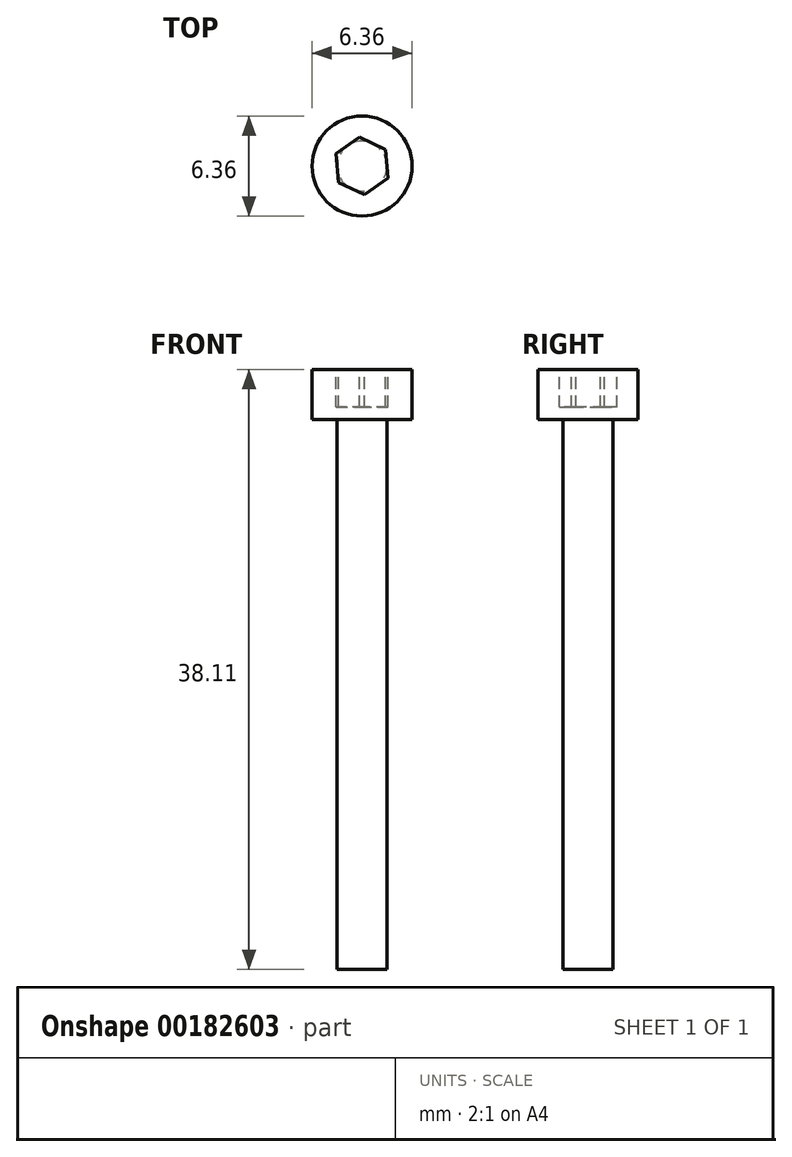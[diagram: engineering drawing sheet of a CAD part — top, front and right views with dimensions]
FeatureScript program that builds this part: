
annotation { "Feature Type Name" : "Feature", "Feature Type Description" : "" }
export const myFeature = defineFeature(function(context is Context, id is Id, definition is map)
    precondition{}
    {
        {
            var Q0;
            Q0=qCreatedBy(makeId("Top.planeOp"),FACE);
            var sketch = newSketch(context, id + "F0", { "sketchPlane" : qUnion([Q0])});
            skCircle(sketch, "E0", {"center": v(0, 0) * mm, "radius": 3.18 * mm});
            skSolve(sketch);
        }
        {
            var Q0;
            Q0 = qSketchRegion(id + "F0", true);
            extrude(context, id + "F1", {"entities" : qUnion([Q0]), "depth" : 3.17 * mm});
        }
        {
            var Q0;
            Q0=makeQuery(id+"F1.opExtrude","CAP_FACE",FACE,{"disambiguationData":[OSD([sQuery(id+"F0.wireOp",EDGE,"E0")])],"isStart":true});
            var sketch = newSketch(context, id + "F2", { "sketchPlane" : qUnion([Q0])});
            skCircle(sketch, "E1", {"center": v(0, 0) * mm, "radius": 1.59 * mm});
            skSolve(sketch);
        }
        {
            var Q0;
            Q0 = qSketchRegion(id + "F2", true);
            extrude(context, id + "F3", {"entities" : qUnion([Q0]), "operationType" : NewBodyOperationType.ADD, "depth" : 34.92 * mm});
        }
        {
            var Q0;
            Q0=makeQuery(id+"F1.opExtrude","CAP_FACE",FACE,{"disambiguationData":[OSD([sQuery(id+"F0.wireOp",EDGE,"E0")])],"isStart":false});
            var sketch = newSketch(context, id + "F4", { "sketchPlane" : qUnion([Q0])});
            skCircle(sketch, "E2.cCircle", {"center": v(0, 0) * mm, "radius": 1.59 * mm, "construction": true});
            skLineSegment(sketch, "E2.0", {"start": v(-0.16, 1.83) * mm, "end": v(1.5, 1.05) * mm});
            skLineSegment(sketch, "E2.1", {"start": v(1.5, 1.05) * mm, "end": v(1.66, -0.78) * mm});
            skLineSegment(sketch, "E2.2", {"start": v(1.66, -0.78) * mm, "end": v(0.16, -1.83) * mm});
            skLineSegment(sketch, "E2.3", {"start": v(0.16, -1.83) * mm, "end": v(-1.5, -1.05) * mm});
            skLineSegment(sketch, "E2.4", {"start": v(-1.5, -1.05) * mm, "end": v(-1.66, 0.78) * mm});
            skLineSegment(sketch, "E2.5", {"start": v(-1.66, 0.78) * mm, "end": v(-0.16, 1.83) * mm});
            skPoint(sketch, "E2.0.midPoint", {"position": v(0.67, 1.44) * mm});
            skSolve(sketch);
        }
        {
            var Q0;
            Q0 = qSketchRegion(id + "F4", true);
            extrude(context, id + "F5", {"entities" : qUnion([Q0]), "operationType" : NewBodyOperationType.REMOVE, "oppositeDirection" : true, "depth" : 2.38 * mm});
        }
    });
